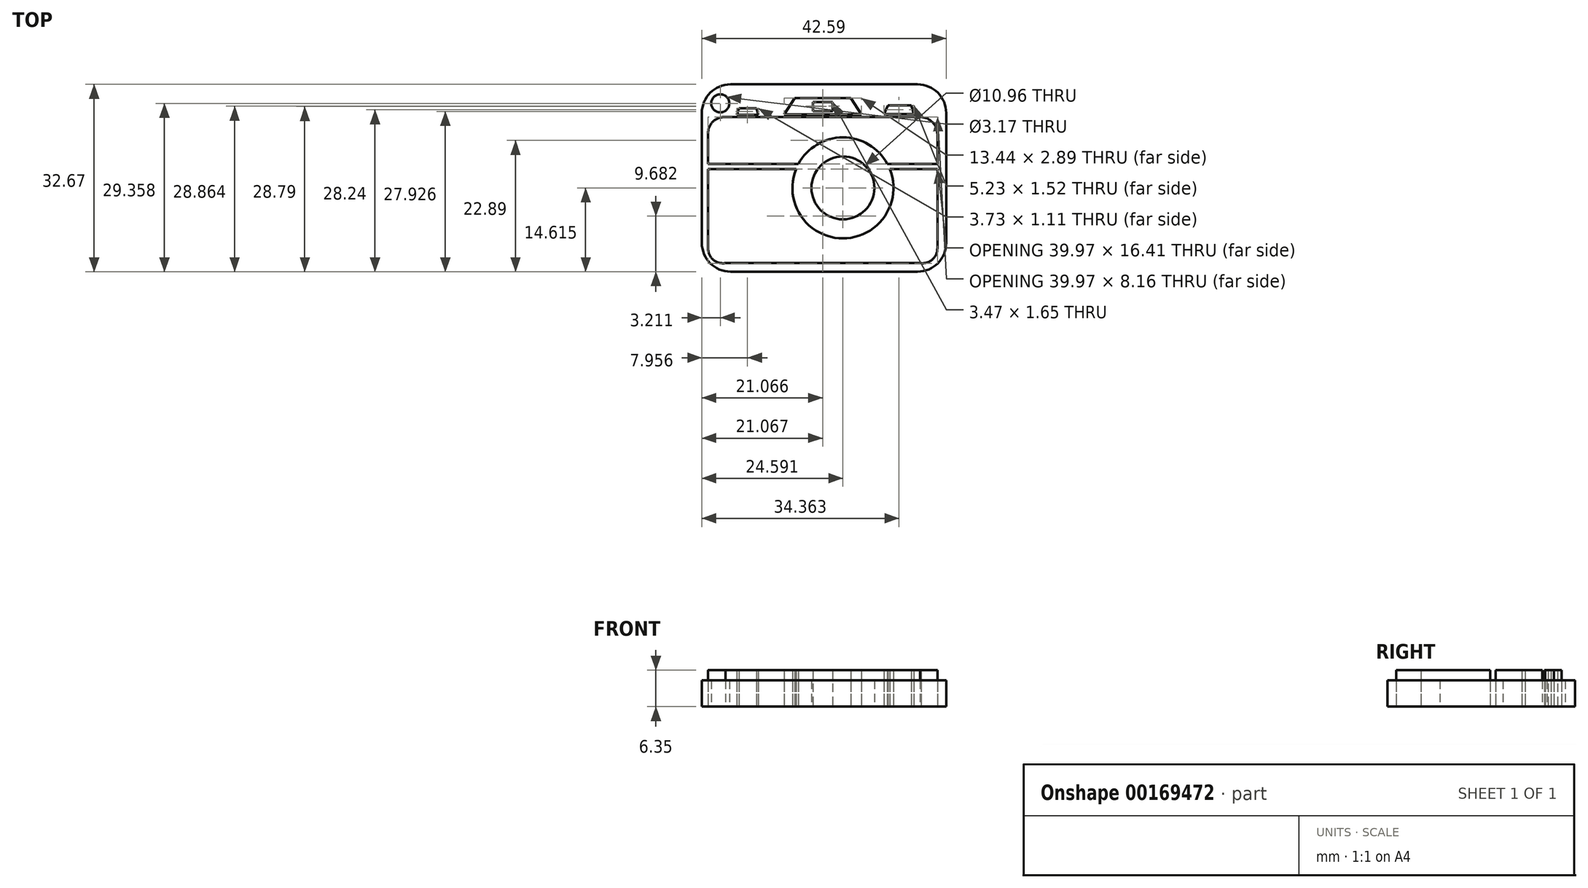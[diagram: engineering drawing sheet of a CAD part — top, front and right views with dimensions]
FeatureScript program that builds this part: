
annotation { "Feature Type Name" : "Feature", "Feature Type Description" : "" }
export const myFeature = defineFeature(function(context is Context, id is Id, definition is map)
    precondition{}
    {
        {
            var Q0;
            Q0=qCreatedBy(makeId("Top.planeOp"),FACE);
            var sketch = newSketch(context, id + "F0", { "sketchPlane" : qUnion([Q0])});
            skLineSegment(sketch, "E0", {"start": v(-2.3, 9.86) * mm, "end": v(-7.17, 9.86) * mm});
            skLineSegment(sketch, "E1", {"start": v(-7.17, 9.86) * mm, "end": v(-9.02, 6.97) * mm});
            skLineSegment(sketch, "E2", {"start": v(-9.02, 6.97) * mm, "end": v(-2.3, 6.97) * mm});
            skLineSegment(sketch, "E3.bottom", {"start": v(-2.3, 9.16) * mm, "end": v(-4.03, 9.16) * mm});
            skLineSegment(sketch, "E3.top", {"start": v(-2.3, 7.52) * mm, "end": v(-4.03, 7.52) * mm});
            skLineSegment(sketch, "E3.right", {"start": v(-4.03, 9.16) * mm, "end": v(-4.03, 7.52) * mm});
            skLineSegment(sketch, "E4", {"start": v(-16.9, 8.03) * mm, "end": v(-17.27, 6.92) * mm});
            skLineSegment(sketch, "E5", {"start": v(-17.27, 6.92) * mm, "end": v(-16.56, 6.92) * mm});
            skLineSegment(sketch, "E6", {"start": v(-13.54, 6.92) * mm, "end": v(-13.8, 8.03) * mm});
            skLineSegment(sketch, "E7", {"start": v(-13.8, 8.03) * mm, "end": v(-16.9, 8.03) * mm});
            skLineSegment(sketch, "E8", {"start": v(-22.28, 3.55) * mm, "end": v(-22.28, -1.64) * mm});
            skArc(sketch, "E9", {"start": v(-22.28, -16.4) * mm, "mid": v(-21.35, -18.38) * mm, "end": v(-19.24, -18.94) * mm});
            skLineSegment(sketch, "E10", {"start": v(-19.24, -18.94) * mm, "end": v(-2.3, -18.94) * mm});
            skLineSegment(sketch, "E11.MirrorCS", {"start": v(-2.3, 9.86) * mm, "end": v(2.58, 9.86) * mm});
            skLineSegment(sketch, "E12.MirrorCS", {"start": v(-2.3, 9.16) * mm, "end": v(-0.56, 9.16) * mm});
            skLineSegment(sketch, "E13.MirrorCS", {"start": v(-0.56, 9.16) * mm, "end": v(-0.56, 7.52) * mm});
            skLineSegment(sketch, "E14.MirrorCS", {"start": v(-2.3, 7.52) * mm, "end": v(-0.56, 7.52) * mm});
            skLineSegment(sketch, "E15.MirrorCS", {"start": v(4.43, 6.97) * mm, "end": v(-2.3, 6.97) * mm});
            skLineSegment(sketch, "E16.MirrorCS", {"start": v(2.58, 9.86) * mm, "end": v(4.43, 6.97) * mm});
            skLineSegment(sketch, "E17.MirrorCS", {"start": v(17.7, 3.55) * mm, "end": v(17.7, -1.64) * mm});
            skLineSegment(sketch, "E18.MirrorCS", {"start": v(14.65, -18.94) * mm, "end": v(-2.3, -18.94) * mm});
            skLineSegment(sketch, "E19", {"start": v(8.39, 7.03) * mm, "end": v(9.44, 7.03) * mm});
            skLineSegment(sketch, "E20", {"start": v(13.62, 7.03) * mm, "end": v(13.13, 8.55) * mm});
            skLineSegment(sketch, "E21", {"start": v(13.13, 8.55) * mm, "end": v(9.07, 8.55) * mm});
            skLineSegment(sketch, "E22", {"start": v(9.07, 8.55) * mm, "end": v(8.39, 7.03) * mm});
            skCircle(sketch, "E23", {"center": v(1.23, -5.84) * mm, "radius": 5.48 * mm});
            skArc(sketch, "E24", {"start": v(-6.95, -2.56) * mm, "mid": v(1.23, -14.64) * mm, "end": v(9.4, -2.56) * mm});
            skLineSegment(sketch, "E25", {"start": v(-6.51, -1.64) * mm, "end": v(-22.28, -1.64) * mm});
            skLineSegment(sketch, "E26", {"start": v(-22.28, -2.56) * mm, "end": v(-6.95, -2.56) * mm});
            skLineSegment(sketch, "E27", {"start": v(8.97, -1.64) * mm, "end": v(17.7, -1.64) * mm});
            skLineSegment(sketch, "E28", {"start": v(9.4, -2.56) * mm, "end": v(17.7, -2.56) * mm});
            skArc(sketch, "E29.trimOffspring", {"start": v(8.97, -1.64) * mm, "mid": v(1.23, 2.97) * mm, "end": v(-6.51, -1.64) * mm});
            skLineSegment(sketch, "E30.trimOffspring", {"start": v(-22.28, -2.56) * mm, "end": v(-22.28, -16.4) * mm});
            skLineSegment(sketch, "E31.trimOffspring", {"start": v(17.7, -2.56) * mm, "end": v(17.7, -16.4) * mm});
            skLineSegment(sketch, "E32.trimOffspring", {"start": v(12.5, 7.03) * mm, "end": v(13.62, 7.03) * mm});
            skLineSegment(sketch, "E33.trimOffspring", {"start": v(-14.15, 6.92) * mm, "end": v(-13.54, 6.92) * mm});
            skLineSegment(sketch, "E34", {"start": v(9.44, 7.03) * mm, "end": v(12.5, 7.03) * mm});
            skLineSegment(sketch, "E35", {"start": v(-16.56, 6.92) * mm, "end": v(-14.15, 6.92) * mm});
            skLineSegment(sketch, "E36.bottom", {"start": v(-18.36, 12.22) * mm, "end": v(14.23, 12.22) * mm});
            skLineSegment(sketch, "E36.top", {"start": v(-18.36, -20.45) * mm, "end": v(14.23, -20.45) * mm});
            skLineSegment(sketch, "E36.left", {"start": v(-23.36, 7.22) * mm, "end": v(-23.36, -15.45) * mm});
            skLineSegment(sketch, "E36.right", {"start": v(19.23, 7.22) * mm, "end": v(19.23, -15.45) * mm});
            skPoint(sketch, "E37.visualSharp", {"position": v(-23.36, 12.22) * mm});
            skArc(sketch, "E37.filletArc", {"start": v(-18.36, 12.22) * mm, "mid": v(-21.9, 10.75) * mm, "end": v(-23.36, 7.22) * mm});
            skPoint(sketch, "E38.visualSharp", {"position": v(19.23, 12.22) * mm});
            skArc(sketch, "E38.filletArc", {"start": v(19.23, 7.22) * mm, "mid": v(17.76, 10.75) * mm, "end": v(14.23, 12.22) * mm});
            skPoint(sketch, "E39.visualSharp", {"position": v(19.23, -20.45) * mm});
            skArc(sketch, "E39.filletArc", {"start": v(14.23, -20.45) * mm, "mid": v(17.76, -18.98) * mm, "end": v(19.23, -15.45) * mm});
            skPoint(sketch, "E40.visualSharp", {"position": v(-23.36, -20.45) * mm});
            skArc(sketch, "E40.filletArc", {"start": v(-23.36, -15.45) * mm, "mid": v(-21.9, -18.98) * mm, "end": v(-18.36, -20.45) * mm});
            skCircle(sketch, "E41", {"center": v(-20.15, 8.9) * mm, "radius": 1.59 * mm});
            skArc(sketch, "E42", {"start": v(14.65, -18.94) * mm, "mid": v(16.77, -18.37) * mm, "end": v(17.7, -16.4) * mm});
            skLineSegment(sketch, "E43", {"start": v(-19.45, 6.52) * mm, "end": v(14.87, 6.52) * mm});
            skArc(sketch, "E44", {"start": v(-19.45, 6.52) * mm, "mid": v(-21.5, 5.64) * mm, "end": v(-22.28, 3.55) * mm});
            skArc(sketch, "E45", {"start": v(17.7, 3.55) * mm, "mid": v(16.87, 5.6) * mm, "end": v(14.87, 6.52) * mm});
            skSolve(sketch);
        }
        {
            var Q0;
            Q0=makeQuery(id+"F0.imprint","IMPRINT",FACE,{"disambiguationData":[TD([[makeQuery(id+"F0.imprint","IMPRINT",EDGE,{"derivedFrom":sQuery(id+"F0.wireOp",EDGE,"E8")}),1.0]])]});
            var Q1;
            Q1=makeQuery(id+"F0.imprint","IMPRINT",FACE,{"disambiguationData":[TD([[makeQuery(id+"F0.imprint","IMPRINT",EDGE,{"derivedFrom":sQuery(id+"F0.wireOp",EDGE,"E9")}),1.0]])]});
            var Q2;
            Q2=makeQuery(id+"F0.imprint","IMPRINT",FACE,{"disambiguationData":[TD([[makeQuery(id+"F0.imprint","IMPRINT",EDGE,{"derivedFrom":sQuery(id+"F0.wireOp",EDGE,"E0")}),1.0]])]});
            var Q3;
            Q3=makeQuery(id+"F0.imprint","IMPRINT",FACE,{"disambiguationData":[TD([[makeQuery(id+"F0.imprint","IMPRINT",EDGE,{"derivedFrom":sQuery(id+"F0.wireOp",EDGE,"E4")}),1.0]])]});
            var Q4;
            Q4=makeQuery(id+"F0.imprint","IMPRINT",FACE,{"disambiguationData":[TD([[makeQuery(id+"F0.imprint","IMPRINT",EDGE,{"derivedFrom":sQuery(id+"F0.wireOp",EDGE,"E19")}),1.0]])]});
            extrude(context, id + "F1", {"entities" : qUnion([Q0, Q1, Q2, Q3, Q4]), "depth" : 6.35 * mm});
        }
        {
            var Q0;
            Q0=makeQuery(id+"F0.imprint","IMPRINT",FACE,{"disambiguationData":[TD([[makeQuery(id+"F0.imprint","IMPRINT",EDGE,{"derivedFrom":sQuery(id+"F0.wireOp",EDGE,"E0")}),-1.0]])]});
            extrude(context, id + "F2", {"entities" : qUnion([Q0]), "depth" : 4.57 * mm});
        }
    });
